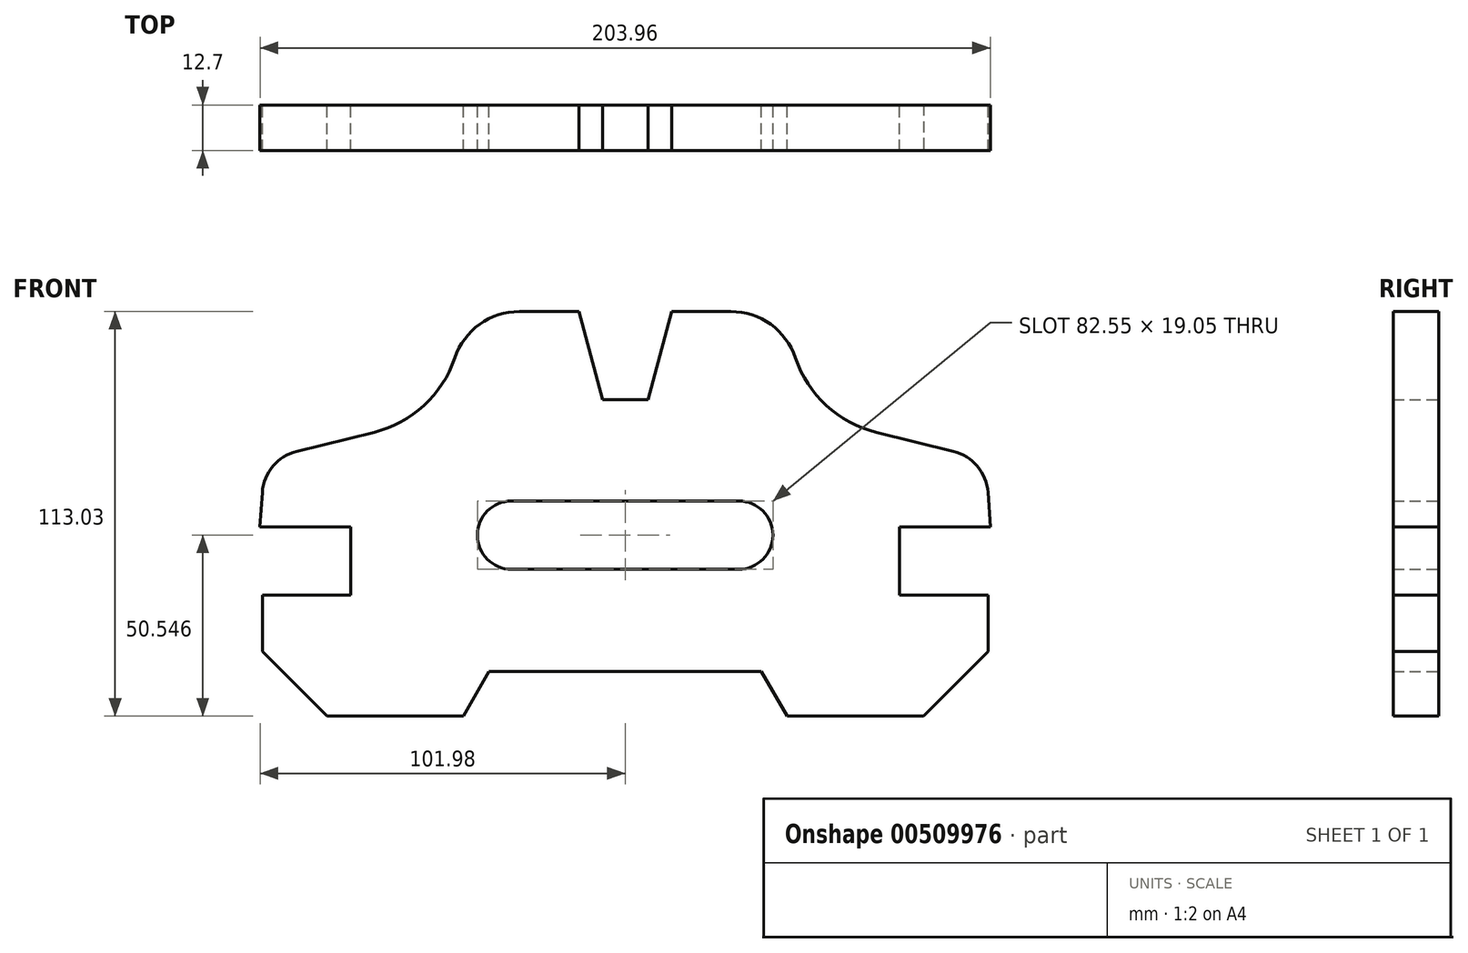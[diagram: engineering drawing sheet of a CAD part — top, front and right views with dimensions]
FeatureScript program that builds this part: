
annotation { "Feature Type Name" : "Feature", "Feature Type Description" : "" }
export const myFeature = defineFeature(function(context is Context, id is Id, definition is map)
    precondition{}
    {
        {
            var Q0;
            Q0=qCreatedBy(makeId("Front.planeOp"),FACE);
            var sketch = newSketch(context, id + "F0", { "sketchPlane" : qUnion([Q0])});
            skLineSegment(sketch, "E0", {"start": v(-38.03, -61.53) * mm, "end": v(-45.21, -73.98) * mm});
            skLineSegment(sketch, "E1", {"start": v(-45.21, -73.98) * mm, "end": v(-101.35, -73.98) * mm});
            skLineSegment(sketch, "E2", {"start": v(-101.35, -40.2) * mm, "end": v(-76.58, -40.2) * mm});
            skLineSegment(sketch, "E3", {"start": v(-76.58, -40.2) * mm, "end": v(-76.58, -21.15) * mm});
            skLineSegment(sketch, "E4", {"start": v(-76.58, -21.15) * mm, "end": v(-101.98, -21.15) * mm});
            skLineSegment(sketch, "E5", {"start": v(-101.98, -21.15) * mm, "end": v(-101.35, -11.5) * mm});
            skArc(sketch, "E6", {"start": v(-101.35, -11.5) * mm, "mid": v(-98.4, -4.17) * mm, "end": v(-91.7, 0) * mm});
            skLineSegment(sketch, "E7", {"start": v(-91.7, 0) * mm, "end": v(-70.1, 5.31) * mm});
            skArc(sketch, "E8", {"start": v(-70.1, 5.31) * mm, "mid": v(-56.18, 12.79) * mm, "end": v(-47.58, 26.05) * mm});
            skArc(sketch, "E9", {"start": v(-47.58, 26.05) * mm, "mid": v(-40.64, 35.46) * mm, "end": v(-29.52, 39.05) * mm});
            skLineSegment(sketch, "E10", {"start": v(-29.52, 39.05) * mm, "end": v(-12.95, 39.05) * mm});
            skLineSegment(sketch, "E11", {"start": v(-12.95, 39.05) * mm, "end": v(-6.35, 14.41) * mm});
            skArc(sketch, "E12.MirrorCS", {"start": v(70.1, 5.31) * mm, "mid": v(56.18, 12.79) * mm, "end": v(47.58, 26.05) * mm});
            skArc(sketch, "E13.MirrorCS", {"start": v(101.35, -11.5) * mm, "mid": v(98.4, -4.17) * mm, "end": v(91.7, 0) * mm});
            skLineSegment(sketch, "E14.MirrorCS", {"start": v(91.7, 0) * mm, "end": v(70.1, 5.31) * mm});
            skLineSegment(sketch, "E15.MirrorCS", {"start": v(76.58, -21.15) * mm, "end": v(101.98, -21.15) * mm});
            skLineSegment(sketch, "E16.MirrorCS", {"start": v(101.98, -21.15) * mm, "end": v(101.35, -11.5) * mm});
            skLineSegment(sketch, "E17.MirrorCS", {"start": v(38.03, -61.53) * mm, "end": v(45.21, -73.98) * mm});
            skArc(sketch, "E18.MirrorCS", {"start": v(47.58, 26.05) * mm, "mid": v(40.64, 35.46) * mm, "end": v(29.52, 39.05) * mm});
            skLineSegment(sketch, "E19.MirrorCS", {"start": v(47.58, 26.05) * mm, "end": v(47.58, 26.05) * mm});
            skLineSegment(sketch, "E20.MirrorCS", {"start": v(76.58, -40.2) * mm, "end": v(76.58, -21.15) * mm});
            skLineSegment(sketch, "E21.MirrorCS", {"start": v(101.35, -40.2) * mm, "end": v(76.58, -40.2) * mm});
            skLineSegment(sketch, "E22.MirrorCS", {"start": v(45.21, -73.98) * mm, "end": v(101.35, -73.98) * mm});
            skLineSegment(sketch, "E23.MirrorCS", {"start": v(12.95, 39.05) * mm, "end": v(6.35, 14.41) * mm});
            skLineSegment(sketch, "E24.MirrorCS", {"start": v(29.52, 39.05) * mm, "end": v(12.95, 39.05) * mm});
            skLineSegment(sketch, "E25", {"start": v(-6.35, 14.41) * mm, "end": v(6.35, 14.41) * mm});
            skLineSegment(sketch, "E26", {"start": v(-38.03, -61.53) * mm, "end": v(38.03, -61.53) * mm});
            skLineSegment(sketch, "E27", {"start": v(-38.03, -61.53) * mm, "end": v(-38.03, -93.09) * mm, "construction": true});
            skLineSegment(sketch, "E28", {"start": v(-6.35, 14.41) * mm, "end": v(-6.35, 45.47) * mm, "construction": true});
            skLineSegment(sketch, "E29", {"start": v(-101.35, -40.2) * mm, "end": v(-101.35, -73.98) * mm});
            skLineSegment(sketch, "E30", {"start": v(101.35, -40.2) * mm, "end": v(101.35, -73.98) * mm});
            skLineSegment(sketch, "E31.bottom", {"start": v(31.75, -32.96) * mm, "end": v(-31.75, -32.96) * mm});
            skLineSegment(sketch, "E31.top", {"start": v(31.75, -13.9) * mm, "end": v(-31.75, -13.9) * mm});
            skLineSegment(sketch, "E31.left", {"start": v(31.75, -32.96) * mm, "end": v(31.75, -13.9) * mm});
            skLineSegment(sketch, "E31.right", {"start": v(-31.75, -32.96) * mm, "end": v(-31.75, -13.9) * mm});
            skPoint(sketch, "E31.middle", {"position": v(0, -23.43) * mm});
            skCircle(sketch, "E32", {"center": v(-31.75, -23.43) * mm, "radius": 9.53 * mm});
            skCircle(sketch, "E33", {"center": v(31.75, -23.43) * mm, "radius": 9.53 * mm});
            skSolve(sketch);
        }
        {
            var Q0;
            Q0=makeQuery(id+"F0.imprint","IMPRINT",FACE,{"disambiguationData":[TD([[makeQuery(id+"F0.imprint","IMPRINT",EDGE,{"derivedFrom":sQuery(id+"F0.wireOp",EDGE,"E0")}),-1.0]])]});
            extrude(context, id + "F1", {"entities" : qUnion([Q0]), "depth" : 12.7 * mm, "offsetDistance" : 25.4 * mm});
        }
        {
            var Q0;
            Q0=makeQuery(id+"F1.opExtrude","SWEPT_EDGE",EDGE,{"disambiguationData":[OSD([sQuery(id+"F0.wireOp",EDGE,"E1"),sQuery(id+"F0.wireOp",EDGE,"E29")])]});
            var Q1;
            Q1=makeQuery(id+"F1.opExtrude","SWEPT_EDGE",EDGE,{"disambiguationData":[OSD([sQuery(id+"F0.wireOp",EDGE,"E22.MirrorCS"),sQuery(id+"F0.wireOp",EDGE,"E30")])]});
            chamfer(context, id + "F2", {"entities" : qUnion([Q0, Q1]), "width" : 18.03 * mm, "tangentPropagation" : true});
        }
    });
